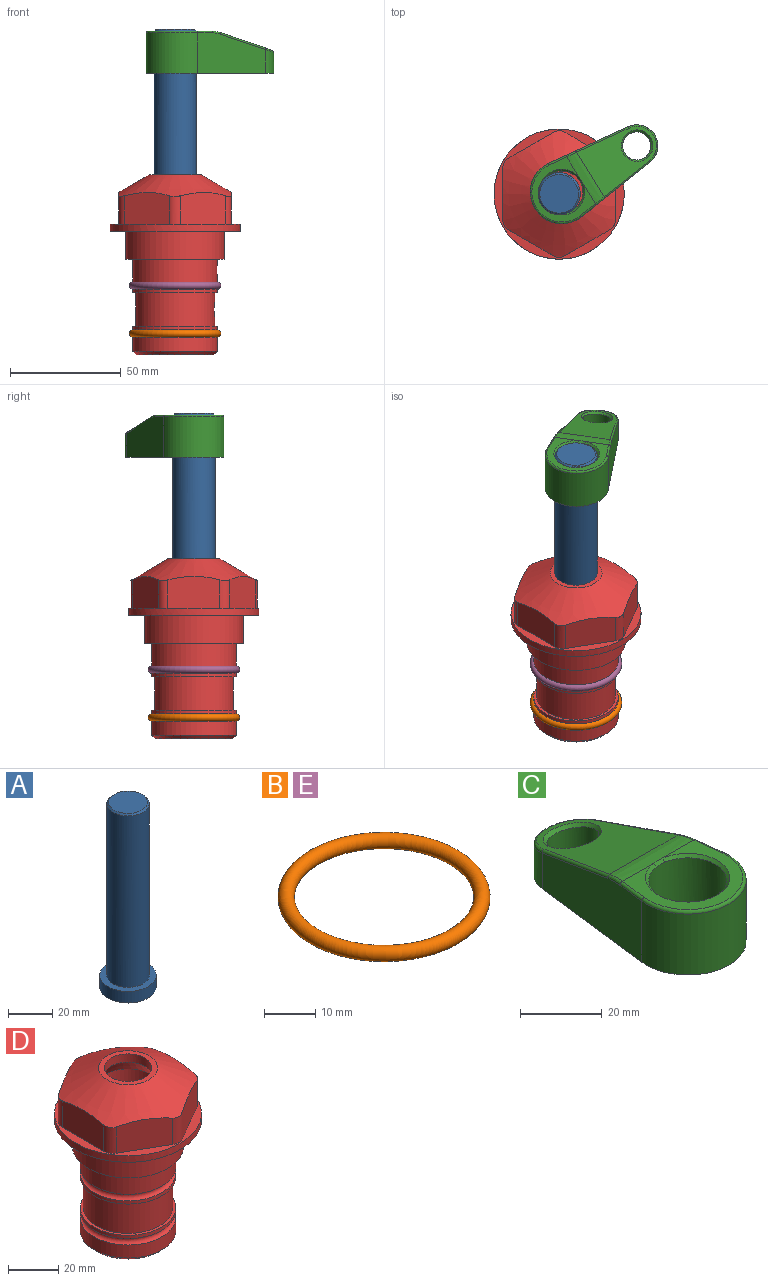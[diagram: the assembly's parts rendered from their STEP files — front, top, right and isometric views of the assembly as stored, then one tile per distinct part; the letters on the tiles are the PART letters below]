
ASSEMBLY  parts=5 mates=4
PART A: 6 faces, bbox 25.4x25.4x101.6 mm
  f0: plane 17.46x17.46mm, normal (0,0,1), area 239.5mm2, adj f5
  f1: plane 25.4x25.4mm, normal (0,0,-1), area 506.7mm2, adj f2
  f2: cylinder r=12.7mm len=25.4mm, axis (0,0,1), area 506.7mm2, adj f1,f3
  f3: plane 25.4x25.4mm, normal (0,0,1), area 221.7mm2, adj f2,f4
  f4: cylinder r=9.53mm len=94.46mm, axis (0,0,1), area 5653mm2, adj f3,f5
  f5: cone r=8.73mm half-angle=45deg, axis (0,0,-1), area 64.4mm2, adj f0,f4
PART B: 1 faces, bbox 44.7x44.7x3.2 mm
  f0: torus R=19.05mm, axis (0,0,1), area 1193.9mm2
PART C: 31 faces, bbox 31.7x65.5x19.8 mm
  f0: plane 39.12x18.26mm, normal (0.99,0.12,0), area 612.2mm2, adj f1,f4,f7,f11,f13,f15
  f1: cylinder r=9.53mm len=18.91mm, axis (0,0,-1), area 296.1mm2, adj f0,f2,f7,f17
  f2: plane 39.12x18.26mm, normal (-0.99,0.12,0), area 612.2mm2, adj f1,f4,f7,f12,f14,f16
  f3: cylinder r=6.35mm len=12.7mm, axis (0,0,-1), area 362.4mm2, adj f7,f18
  f4: cylinder r=14.29mm len=28.58mm, axis (0,0,-1), area 882.2mm2, adj f0,f2,f7,f10
  f5: cylinder r=9.53mm len=19.05mm, axis (0,0,-1), area 1092.6mm2, adj f7,f19,f20
  f6: plane 26.99x23.69mm, normal (0,0,1), area 216.2mm2, adj f9,f10,f11,f12,f19
  f7: plane 63.5x28.58mm, normal (0,0,-1), area 661.8mm2, adj f0,f1,f2,f3,f4,f5,f22,f23
  f8: plane 33.52x23.6mm, normal (0,0.26,0.97), area 486mm2, adj f9,f15,f16,f17,f18
  f9: cylinder r=19.05mm len=24.72mm, axis (1,0,0), area 120.4mm2, adj f6,f8,f13,f14,f20
  f10: torus R=13.49mm, axis (0,0,1), area 59mm2, adj f4,f6,f11,f12
  f11: cylinder r=0.79mm len=8.67mm, axis (0.12,-0.99,0), area 10.8mm2, adj f0,f6,f10,f13
  f12: cylinder r=0.79mm len=8.67mm, axis (0.12,0.99,0), area 10.8mm2, adj f2,f6,f10,f14
  f13: bspline ~4.95x1.42mm, area 6.1mm2, adj f0,f9,f11,f15
  f14: bspline ~4.95x1.42mm, area 6.1mm2, adj f2,f9,f12,f16
  f15: cylinder r=0.79mm len=25.95mm, axis (0.12,-0.96,0.26), area 32.9mm2, adj f0,f8,f13,f17
  f16: cylinder r=0.79mm len=25.95mm, axis (0.12,0.96,-0.26), area 32.9mm2, adj f2,f8,f14,f17
  f17: bspline ~18.91x8.38mm, area 30mm2, adj f1,f8,f15,f16
  f18: bspline ~14.29x14.29mm, area 48.3mm2, adj f3,f8
  f19: cone r=9.53mm half-angle=45deg, axis (0,0,1), area 66.5mm2, adj f5,f6,f20
  f20: bspline ~3.22x0.96mm, area 3.5mm2, adj f5,f9,f19
  f21: plane 2.75x2.72mm, normal (0,0,-1), area 2.9mm2, adj f23,f25,f28
  f22: plane 23.05x15.88mm, normal (-0.99,-0.12,0), area 323.6mm2, adj f7,f25,f26,f27,f28,f29
  f23: plane 23.05x15.88mm, normal (0.99,-0.12,0), area 323.6mm2, adj f7,f21,f25,f27,f28,f30
  f24: cylinder r=9.53mm len=10.69mm, axis (0,0,-1), area 114.7mm2, adj f7,f27,f29,f30
  f25: cylinder r=12.7mm len=20.59mm, axis (0,0,-1), area 381.1mm2, adj f7,f21,f22,f23,f26,f28
  f26: plane 2.75x2.72mm, normal (0,0,-1), area 2.9mm2, adj f22,f25,f28
  f27: plane 19.72x18.37mm, normal (0,-0.26,-0.97), area 291.8mm2, adj f22,f23,f24,f28,f29,f30
  f28: cylinder r=15.88mm len=19.92mm, axis (1,0,0), area 54.8mm2, adj f21,f22,f23,f25,f26,f27
  f29: cylinder r=1.59mm len=11mm, axis (0,0,-1), area 34.7mm2, adj f7,f22,f24,f27
  f30: cylinder r=1.59mm len=11mm, axis (0,0,-1), area 34.7mm2, adj f7,f23,f24,f27
PART D: 36 faces, bbox 58.7x58.7x81 mm
  f0: cylinder r=17.78mm len=35.56mm, axis (0,0,1), area 1670.8mm2, adj f23,f24,f31
  f1: cylinder r=19.05mm len=38.1mm, axis (0,0,1), area 1191.9mm2, adj f26,f27,f30
  f2: plane 58.66x58.66mm, normal (0,0,-1), area 1150.6mm2, adj f3,f28
  f3: cylinder r=29.33mm len=58.66mm, axis (0,0,-1), area 585.1mm2, adj f2,f4
  f4: plane 58.66x58.66mm, normal (0,0,1), area 475.9mm2, adj f3,f5,f6,f7,f8,f9,f10,f11
  f5: plane 20.32x14.34mm, normal (-0.5,0.87,0), area 324.4mm2, adj f4,f15,f16,f17
  f6: plane 20.32x14.34mm, normal (0.5,0.87,0), area 324.4mm2, adj f4,f14,f15,f17
  f7: plane 23.48x14.34mm, normal (1,0,0), area 324.4mm2, adj f4,f13,f14,f17
  f8: plane 20.32x14.34mm, normal (0.5,-0.87,0), area 324.4mm2, adj f4,f12,f13,f17
  f9: plane 20.32x14.34mm, normal (-0.5,-0.87,0), area 324.4mm2, adj f4,f11,f12,f17
  f10: plane 23.48x14.34mm, normal (-1,0,0), area 324.4mm2, adj f4,f11,f16,f17
  f11: cylinder r=5.08mm len=12.85mm, axis (0,0,-1), area 67.2mm2, adj f4,f9,f10,f17
  f12: cylinder r=5.08mm len=12.85mm, axis (0,0,-1), area 67.2mm2, adj f4,f8,f9,f17
  f13: cylinder r=5.08mm len=12.85mm, axis (0,0,-1), area 67.2mm2, adj f4,f7,f8,f17
  f14: cylinder r=5.08mm len=12.85mm, axis (0,0,-1), area 67.2mm2, adj f4,f6,f7,f17
  f15: cylinder r=5.08mm len=12.85mm, axis (0,0,-1), area 67.2mm2, adj f4,f5,f6,f17
  f16: cylinder r=5.08mm len=12.85mm, axis (0,0,-1), area 67.2mm2, adj f4,f5,f10,f17
  f17: cone r=11.73mm half-angle=60deg, axis (0,0,-1), area 2071.8mm2, adj f5,f6,f7,f8,f9,f10,f11,f12
  f18: plane 23.46x23.46mm, normal (0,0,1), area 147.4mm2, adj f17,f35
  f19: plane 34.93x34.93mm, normal (0,0,-1), area 958mm2, adj f29
  f20: cylinder r=19.05mm len=38.1mm, axis (0,0,1), area 760.1mm2, adj f21,f29
  f21: torus R=19.05mm, axis (0,0,1), area 565.3mm2, adj f20,f22
  f22: cylinder r=19.05mm len=38.1mm, axis (0,0,1), area 190mm2, adj f21,f23
  f23: plane 38.1x38.1mm, normal (0,0,1), area 146.9mm2, adj f0,f22
  f24: plane 38.1x38.1mm, normal (0,0,-1), area 146.9mm2, adj f0,f25
  f25: cylinder r=19.05mm len=38.1mm, axis (0,0,1), area 190mm2, adj f24,f26
  f26: torus R=19.05mm, axis (0,0,1), area 565.3mm2, adj f1,f25
  f27: plane 44.45x44.45mm, normal (0,0,-1), area 411.7mm2, adj f1,f28
  f28: cylinder r=22.23mm len=44.45mm, axis (0,0,1), area 1773.5mm2, adj f2,f27
  f29: cone r=19.05mm half-angle=45deg, axis (0,0,1), area 257.5mm2, adj f19,f20
  f30: cylinder r=3.17mm len=6.75mm, axis (-1,0,0), area 128mm2, adj f1,f33
  f31: cylinder r=3.17mm len=6.35mm, axis (-1,0,0), area 102.5mm2, adj f0,f33
  f32: plane 25.4x25.4mm, normal (0,0,1), area 506.7mm2, adj f33
  f33: cylinder r=12.7mm len=66.42mm, axis (0,0,-1), area 5236.2mm2, adj f30,f31,f32,f34
  f34: cone r=9.53mm half-angle=30deg, axis (0,0,-1), area 443.4mm2, adj f33,f35
  f35: cylinder r=9.53mm len=19.05mm, axis (0,0,-1), area 240.9mm2, adj f18,f34
PART E: same geometry as B
PLACE A rot(axis=(0,0,-1),58.3deg) t=(0,0,27.55)mm
PLACE B t=(0,0,-21.59)mm
PLACE C rot(axis=(0,0,-1),58.3deg) t=(1.22,0.75,26.76)mm
PLACE D at identity fixed
PLACE E at identity
MATE fastened A.f2 <-> C.f6  axis (0,0,1) through (0,0,90.26)mm
MATE fastened E.f0 <-> D.f0  axis (0,0,1) through (0,0,-24.51)mm
MATE fastened B.f0 <-> D.f0  axis (0,0,1) through (0,0,-46.1)mm
MATE cylindrical A.f2 <-> D.f0  axis (0,0,-1) through (0,0,-10.55)mm
